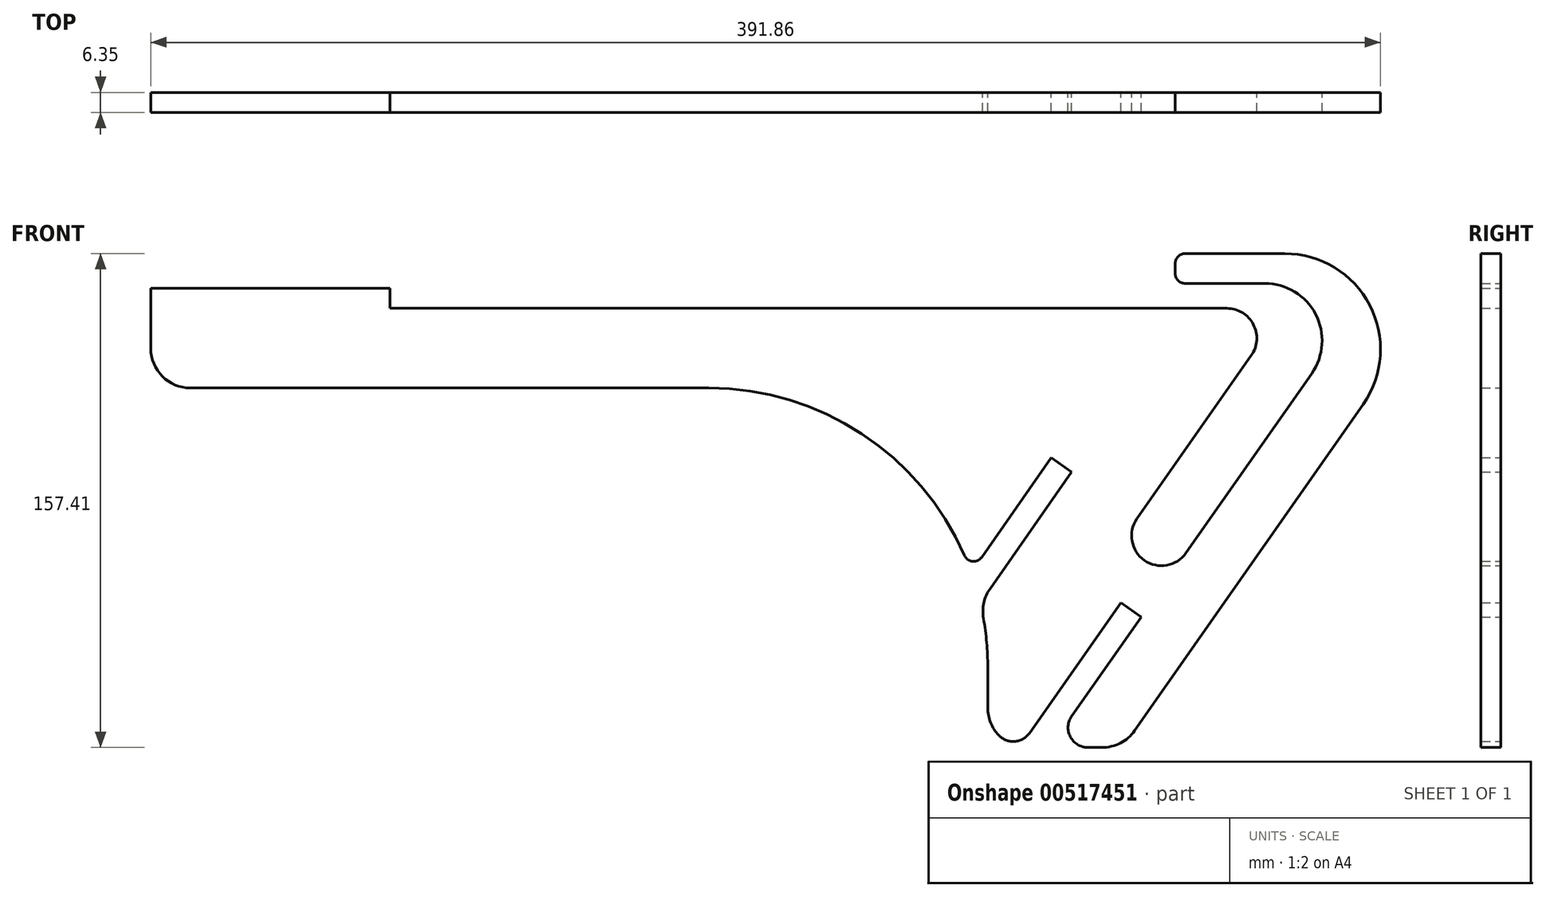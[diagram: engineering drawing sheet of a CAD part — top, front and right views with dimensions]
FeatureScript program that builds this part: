
annotation { "Feature Type Name" : "Feature", "Feature Type Description" : "" }
export const myFeature = defineFeature(function(context is Context, id is Id, definition is map)
    precondition{}
    {
        {
            var Q0;
            Q0=qCreatedBy(makeId("Front.planeOp"),FACE);
            var sketch = newSketch(context, id + "F0", { "sketchPlane" : qUnion([Q0])});
            skLineSegment(sketch, "E0", {"start": v(-6.43, 4.65) * mm, "end": v(22.64, 46.17) * mm});
            skLineSegment(sketch, "E1", {"start": v(22.64, 46.17) * mm, "end": v(29.14, 41.61) * mm});
            skLineSegment(sketch, "E2", {"start": v(27.05, 5.42) * mm, "end": v(99.9, 109.45) * mm});
            skLineSegment(sketch, "E3", {"start": v(-286.46, 139.95) * mm, "end": v(-286.46, 127.25) * mm});
            skLineSegment(sketch, "E4", {"start": v(-273.76, 114.55) * mm, "end": v(-108.66, 114.55) * mm});
            skLineSegment(sketch, "E5", {"start": v(29.14, 41.61) * mm, "end": v(7, 10) * mm});
            skLineSegment(sketch, "E6", {"start": v(12.2, 0) * mm, "end": v(16.64, 0) * mm});
            skArc(sketch, "E7.filletArc", {"start": v(-19.76, 25.65) * mm, "mid": v(-20.1, 33.42) * mm, "end": v(-21.12, 41.14) * mm});
            skPoint(sketch, "E8.visualSharp", {"position": v(-286.46, 114.55) * mm});
            skArc(sketch, "E8.filletArc", {"start": v(-286.46, 127.25) * mm, "mid": v(-282.74, 118.27) * mm, "end": v(-273.76, 114.55) * mm});
            skPoint(sketch, "E9.visualSharp", {"position": v(0, 0) * mm});
            skPoint(sketch, "E10.visualSharp", {"position": v(23.26, 0) * mm});
            skArc(sketch, "E10.filletArc", {"start": v(16.64, 0) * mm, "mid": v(22.5, 1.43) * mm, "end": v(27.05, 5.42) * mm});
            skLineSegment(sketch, "E11", {"start": v(-286.46, 139.95) * mm, "end": v(-286.46, 146.3) * mm});
            skLineSegment(sketch, "E12", {"start": v(-286.46, 146.3) * mm, "end": v(-210.26, 146.3) * mm});
            skLineSegment(sketch, "E13", {"start": v(-210.26, 146.3) * mm, "end": v(-210.26, 139.95) * mm});
            skLineSegment(sketch, "E14.trimOffspring", {"start": v(56.44, 139.95) * mm, "end": v(-210.26, 139.95) * mm});
            skLineSegment(sketch, "E15", {"start": v(74.92, 157.41) * mm, "end": v(43.17, 157.41) * mm});
            skLineSegment(sketch, "E16", {"start": v(40, 154.24) * mm, "end": v(40, 151.06) * mm});
            skLineSegment(sketch, "E17", {"start": v(43.17, 147.89) * mm, "end": v(68.57, 147.89) * mm});
            skPoint(sketch, "E18.visualSharp", {"position": v(40, 147.89) * mm});
            skArc(sketch, "E18.filletArc", {"start": v(40, 151.06) * mm, "mid": v(40.93, 148.82) * mm, "end": v(43.17, 147.89) * mm});
            skPoint(sketch, "E19.visualSharp", {"position": v(40, 157.41) * mm});
            skArc(sketch, "E19.filletArc", {"start": v(43.17, 157.41) * mm, "mid": v(40.93, 156.48) * mm, "end": v(40, 154.24) * mm});
            skLineSegment(sketch, "E20", {"start": v(-19.02, 50.64) * mm, "end": v(6.98, 87.77) * mm});
            skLineSegment(sketch, "E21", {"start": v(6.98, 87.77) * mm, "end": v(0.48, 92.32) * mm});
            skLineSegment(sketch, "E22", {"start": v(0.48, 92.32) * mm, "end": v(-21.68, 60.68) * mm});
            skLineSegment(sketch, "E23", {"start": v(43.42, 62.02) * mm, "end": v(83.49, 119.23) * mm});
            skLineSegment(sketch, "E24", {"start": v(79.85, 114.03) * mm, "end": v(64.24, 124.96) * mm, "construction": true});
            skLineSegment(sketch, "E25", {"start": v(64.24, 124.96) * mm, "end": v(27.82, 72.94) * mm});
            skLineSegment(sketch, "E26", {"start": v(27.82, 72.94) * mm, "end": v(43.42, 62.02) * mm, "construction": true});
            skArc(sketch, "E27", {"start": v(27.82, 72.94) * mm, "mid": v(30.16, 59.68) * mm, "end": v(43.42, 62.02) * mm});
            skArc(sketch, "E28", {"start": v(64.24, 124.96) * mm, "mid": v(64.89, 134.82) * mm, "end": v(56.44, 139.95) * mm});
            skPoint(sketch, "E29.visualSharp", {"position": v(56.44, 139.95) * mm});
            skLineSegment(sketch, "E30", {"start": v(-19.76, 12.7) * mm, "end": v(-19.76, 25.65) * mm});
            skPoint(sketch, "E31.visualSharp", {"position": v(-19.76, 0) * mm});
            skArc(sketch, "E31.filletArc", {"start": v(-19.76, 12.7) * mm, "mid": v(-18.84, 7.95) * mm, "end": v(-16.2, 3.89) * mm});
            skArc(sketch, "E32.filletArc", {"start": v(-16.2, 3.89) * mm, "mid": v(-11.14, 1.96) * mm, "end": v(-6.43, 4.65) * mm});
            skArc(sketch, "E33.filletArc", {"start": v(7, 10) * mm, "mid": v(6.57, 3.42) * mm, "end": v(12.2, 0) * mm});
            skArc(sketch, "E34", {"start": v(83.49, 119.23) * mm, "mid": v(84.72, 138.09) * mm, "end": v(68.57, 147.89) * mm});
            skArc(sketch, "E35", {"start": v(99.9, 109.45) * mm, "mid": v(101.96, 141) * mm, "end": v(74.92, 157.41) * mm});
            skArc(sketch, "E36.trimOffspring", {"start": v(-27.2, 61.23) * mm, "mid": v(-59.98, 100.03) * mm, "end": v(-108.66, 114.55) * mm});
            skPoint(sketch, "E37.visualSharp", {"position": v(-25.05, 55.86) * mm});
            skArc(sketch, "E37.filletArc", {"start": v(-27.2, 61.23) * mm, "mid": v(-24.6, 59.34) * mm, "end": v(-21.68, 60.68) * mm});
            skPoint(sketch, "E38.visualSharp", {"position": v(-22.16, 46.15) * mm});
            skArc(sketch, "E38.filletArc", {"start": v(-19.02, 50.64) * mm, "mid": v(-21.02, 46.1) * mm, "end": v(-21.12, 41.14) * mm});
            skSolve(sketch);
        }
        {
            var Q0;
            {var subQ0=sQuery(id+"F0.wireOp",EDGE,"E0");Q0=makeQuery(id+"F0.imprint","IMPRINT",FACE,{"disambiguationData":[TD([[makeQuery(id+"F0.imprint","IMPRINT",EDGE,{"derivedFrom":subQ0}),1.0]])]});}
            extrude(context, id + "F1", {"entities" : qUnion([Q0]), "depth" : 6.35 * mm, "offsetDistance" : 25.4 * mm});
        }
    });
